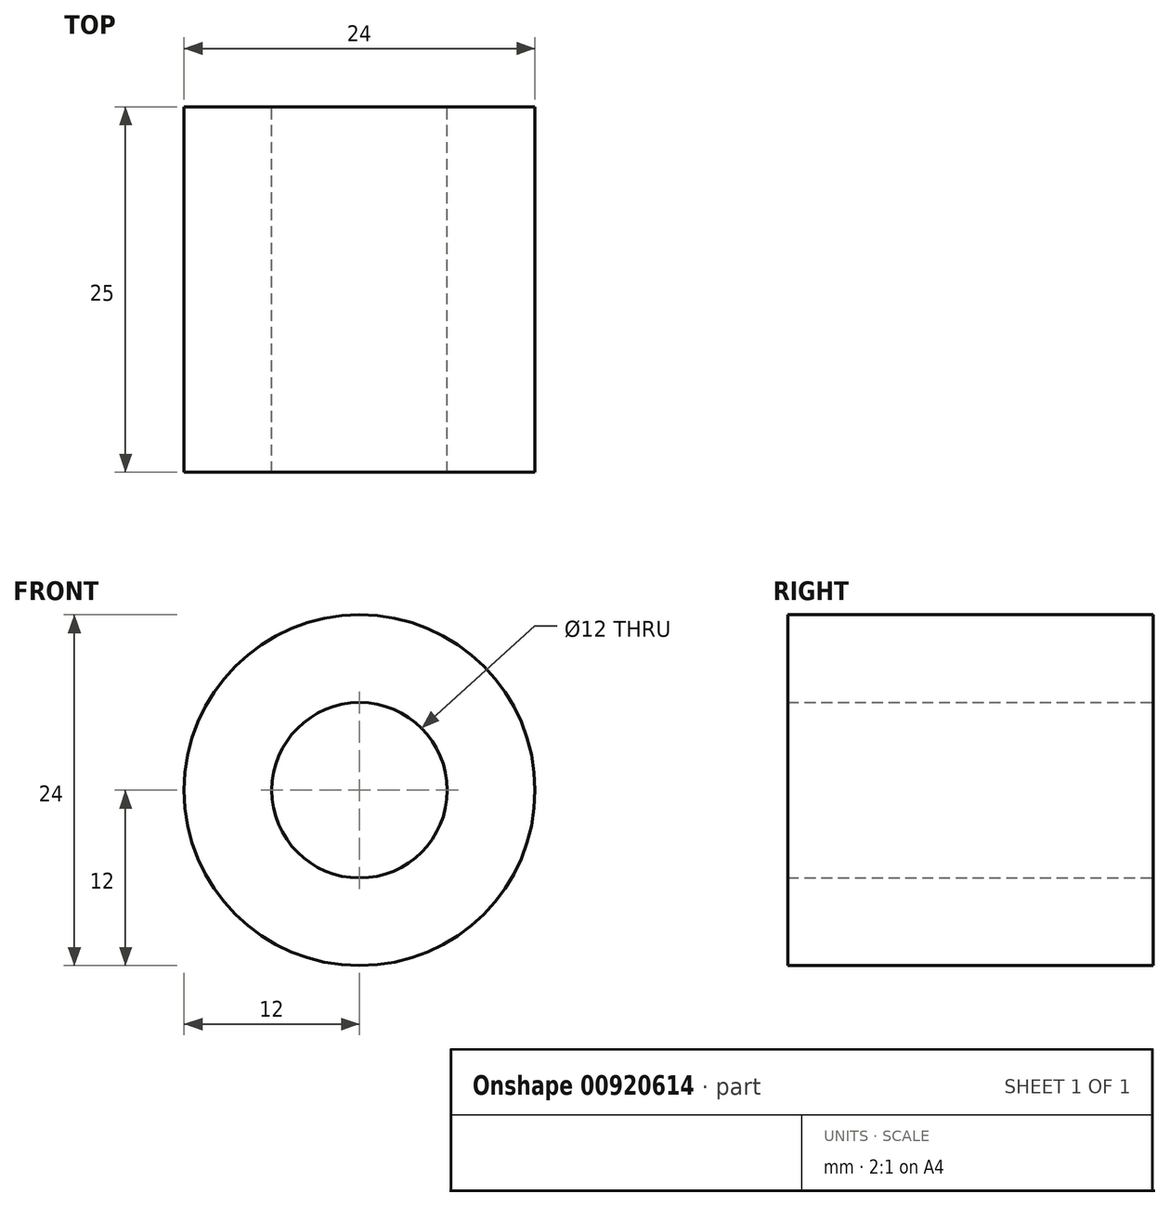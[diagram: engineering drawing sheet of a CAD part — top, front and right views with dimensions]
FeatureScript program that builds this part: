
annotation { "Feature Type Name" : "Feature", "Feature Type Description" : "" }
export const myFeature = defineFeature(function(context is Context, id is Id, definition is map)
    precondition{}
    {
        {
            var Q0;
            Q0=qCreatedBy(makeId("Front.planeOp"),FACE);
            var sketch = newSketch(context, id + "F0", { "sketchPlane" : qUnion([Q0])});
            skCircle(sketch, "E0", {"center": v(0, 0) * mm, "radius": 6 * mm});
            skCircle(sketch, "E1", {"center": v(0, 0) * mm, "radius": 12 * mm});
            skSolve(sketch);
        }
        {
            var Q0;
            Q0=makeQuery(id+"F0.imprint","IMPRINT",FACE,{"disambiguationData":[TD([[makeQuery(id+"F0.imprint","IMPRINT",EDGE,{"derivedFrom":sQuery(id+"F0.wireOp",EDGE,"E0")}),-1.0]])]});
            extrude(context, id + "F1", {"entities" : qUnion([Q0]), "depth" : 25 * mm, "offsetDistance" : 25 * mm});
        }
    });
